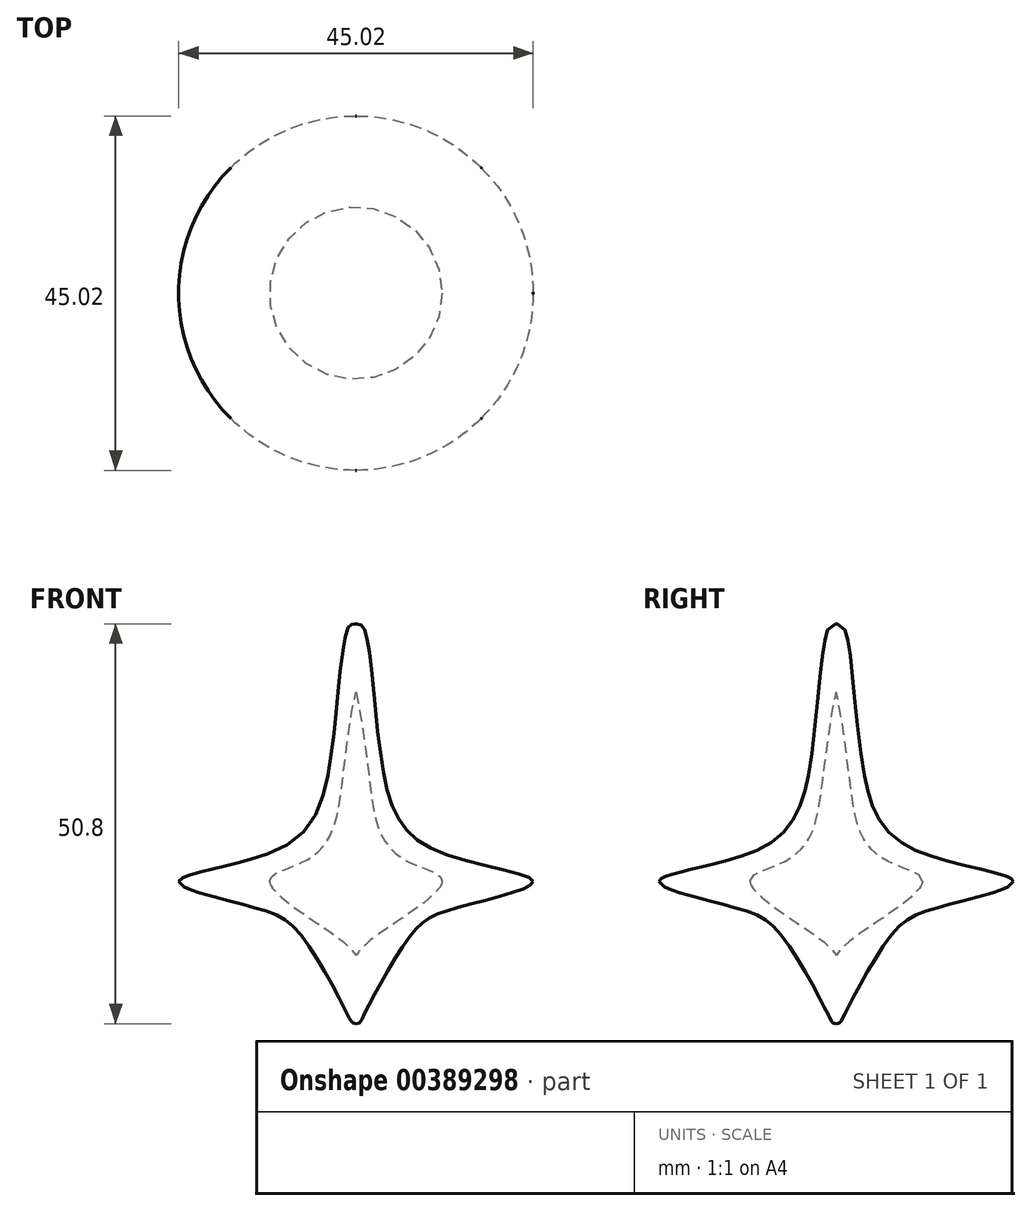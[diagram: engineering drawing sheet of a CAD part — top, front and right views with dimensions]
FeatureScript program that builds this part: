
annotation { "Feature Type Name" : "Feature", "Feature Type Description" : "" }
export const myFeature = defineFeature(function(context is Context, id is Id, definition is map)
    precondition{}
    {
        {
            var Q0;
            Q0=qCreatedBy(makeId("Front.planeOp"),FACE);
            var sketch = newSketch(context, id + "F0", { "sketchPlane" : qUnion([Q0])});
            skLineSegment(sketch, "E0", {"start": v(0, 30.52) * mm, "end": v(0, -20.28) * mm});
            skFitSpline(sketch, "E1", {"points": [v(0, 30.52) * mm, v(1.18, 29.54) * mm, v(3.55, 11.37) * mm, v(10.32, 1.63) * mm, v(22.51, -2.23) * mm, v(12.87, -5.54) * mm, v(6.87, -9.18) * mm, v(0.9, -19.44) * mm, v(0, -20.28) * mm], "startDerivative": vector(34.03, 2.3) * mm, "endDerivative": vector(-31.37, -0.3) * mm});
            skFitSpline(sketch, "E2", {"points": [v(0, 21.83) * mm, v(1.77, 10.16) * mm, v(3.4, 3.35) * mm, v(7.24, 0) * mm, v(10.96, -2.23) * mm, v(2.52, -9.18) * mm, v(0, -11.6) * mm], "startDerivative": vector(10.18, -42.45) * mm, "endDerivative": vector(-12.45, -15.98) * mm});
            skLineSegment(sketch, "E3", {"start": v(22.51, -2.23) * mm, "end": v(0, -2.23) * mm});
            skSolve(sketch);
        }
        {
            var Q0;
            {var subQ0=sQuery(id+"F0.wireOp",EDGE,"E1");var subQ1=sQuery(id+"F0.wireOp",EDGE,"E0");var subQ2=makeQuery(id+"F0.imprint","INTERSECT",VERTEX,{"disambiguationData":[OD(0.0)],"derivedFrom":[subQ1,subQ0]});Q0=makeQuery(id+"F0.imprint","IMPRINT",FACE,{"disambiguationData":[TD([[makeQuery(id+"F0.imprint","IMPRINT",EDGE,{"disambiguationData":[TD([[subQ2,-1.0]])],"derivedFrom":subQ1}),1.0]])]});}
            var Q1;
            {var subQ0=sQuery(id+"F0.wireOp",EDGE,"E1");var subQ1=sQuery(id+"F0.wireOp",EDGE,"E0");var subQ2=makeQuery(id+"F0.imprint","INTERSECT",VERTEX,{"disambiguationData":[OD(1.0)],"derivedFrom":[subQ1,subQ0]});Q1=makeQuery(id+"F0.imprint","IMPRINT",FACE,{"disambiguationData":[TD([[makeQuery(id+"F0.imprint","IMPRINT",EDGE,{"disambiguationData":[TD([[subQ2,1.0]])],"derivedFrom":subQ1}),1.0]])]});}
            var Q2;
            Q2=sQuery(id+"F0.wireOp",EDGE,"E1");
            var Q3;
            Q3=sQuery(id+"F0.wireOp",EDGE,"E0");
            revolve(context, id + "F1", {"entities" : qUnion([Q0, Q1]), "surfaceEntities" : qUnion([Q2]), "axis" : qUnion([Q3]), "revolveType" : RevolveType.FULL});
        }
    });
